# Revit family: Hager-Univers-IP30-D161-Cl.II-FWB-encl--CH-fr
name_source: partatom
category: Equipement électrique
units: mm (PartAtom-declared; Revit-internal decimal feet)

## family parameters
Configuration du panneau = Deux colonnes, circuits au sein
Cote de connecteur circulaire = Utiliser le diamètre
Couper avec des vides une fois chargée = Non
Hôte = Face
Partagée = Non
Point de calcul de pièce = Non
Type d'élément = Tableau de raccordement

## types (19) — shared parameters
Commentaires du type = Univers
EF000003 - mode de pose = EV000384 - saillie
EF000007 - couleur = EV000202 - blanc
EF000049 - profondeur = 161 mm  [stored 0.528215 ft]
EF000116 - numéro RAL = 9010
EF000118 - avec cadre/support de montage = Non
EF001088 - possibilité de montage en saillie = Oui
EF001596 - matériau du boîtier/corps = EV000179 - acier
EF001613 - maintien de fonction = EV000494 - sans
EF002950 - largeur en nombre de modules = 12
EF003532 - convient pour utilisation à l’extérieur = Non
EF004293 - indice de protection contre les chocs (IK) = EV006815 - IK09
EF004464 - type de porte = EV000494 - sans
EF005474 - indice de protection (IP) = EV006410 - IP30
EF006244 - couvercle/porte transparent(e) = Non
EF006306 - avec serrure = Non
EF007800 - adapté à un parafoudre = Non
EF008873 - courant nominal (In) = 125 A
EF015940 - couvercle avec décharge de pression = Non
Fabricant = Hager
HG000002 - avec porte = Non
HG000003 - Gamme = Univers
HG000006 - Encastré = Non
HG000009 - Porte à double battant = Non
HG000010 - Portes asymétriques = Non
HG000023 - Armoire double section = Non
HG000024 - Hauteur de la section basse = 800 mm  [stored 2.62467 ft]
HG000026 - Installation au sol = Non
zero-valued in all types: EF000218 - profondeur d'encastrement, EF000266 - nombre de rangées, Elévation par défaut, HG000027 - Hauteur du socle

## per-type parameters (varying)
| type | EF000008 - largeur | EF000040 - hauteur | EF000339 - type de capot | EF000437 - nombre d'entrées de conduit | EF001131 - profondeur intérieure | EF004427 - nombre de modules | EF009170 - épaisseur de matériau du boîtier | EF009171 - épaisseur de matériau de la porte/du couvercle | EF009212 - finition du couvercle | EF009554 - nombre d'ouvertures pour plaques à bride | HG000004 - Référence fabricant |
| saillie IP30 L1050 H1100 P161  - FWB74D1 | 1050 mm | 1100 mm | EV000494 - sans | 16 | 156 mm  [stored 0.511811 ft] | 336 | 1 mm  [stored 0.00328084 ft] | 1 mm  [stored 0.00328084 ft] | EV009916 - avec échancrure | 8 | FWB74D1 |
| saillie IP30 L1050 H500 P161  - FWB34D1 | 1050 mm | 500 mm  [stored 1.64042 ft] | EV000494 - sans | 16 | 156 mm  [stored 0.511811 ft] | 144 | 1 mm  [stored 0.00328084 ft] | 2 mm  [stored 0.00656168 ft] | EV009916 - avec échancrure | 8 | FWB34D1 |
| saillie IP30 L1050 H650 P161  - FWB44D1 | 1050 mm | 650 mm  [stored 2.13255 ft] | EV004216 - porte | 16 | 160 mm  [stored 0.524934 ft] | 192 | 1 mm  [stored 0.00328084 ft] | 1 mm  [stored 0.00328084 ft] | EV000116 - fermé | 8 | FWB44D1 |
| saillie IP30 L1050 H800 P161  - FWB54D1 | 1050 mm | 800 mm  [stored 2.62467 ft] | EV004216 - porte | 16 | 160 mm  [stored 0.524934 ft] | 240 | 2 mm  [stored 0.00656168 ft] | 1 mm  [stored 0.00328084 ft] | EV009916 - avec échancrure | 8 | FWB54D1 |
| saillie IP30 L1050 H950 P161  - FWB64D1 | 1050 mm | 950 mm  [stored 3.1168 ft] | EV004216 - porte | 16 | 160 mm  [stored 0.524934 ft] | 288 | 2 mm  [stored 0.00656168 ft] | 1 mm  [stored 0.00328084 ft] | EV009916 - avec échancrure | 8 | FWB64D1 |
| saillie IP30 L300 H1100 P161  - FWB71D1 | 300 mm | 1100 mm | EV000494 - sans | 4 | 156 mm  [stored 0.511811 ft] | 84 | 1 mm  [stored 0.00328084 ft] | 1 mm  [stored 0.00328084 ft] | EV009916 - avec échancrure | 2 | FWB71D1 |
| saillie IP30 L300 H1250 P161  - FWB81D1 | 300 mm | 1250 mm  [stored 4.10105 ft] | EV000494 - sans | 4 | 160 mm  [stored 0.524934 ft] | 96 | 1 mm  [stored 0.00328084 ft] | 1 mm  [stored 0.00328084 ft] | EV009916 - avec échancrure | 2 | FWB81D1 |
| saillie IP30 L300 H650 P161  - FWB41D1 | 300 mm | 650 mm  [stored 2.13255 ft] | EV004216 - porte | 4 | 160 mm  [stored 0.524934 ft] | 48 | 1 mm  [stored 0.00328084 ft] | 1 mm  [stored 0.00328084 ft] | EV000116 - fermé | 2 | FWB41D1 |
| saillie IP30 L300 H800 P161  - FWB51D1 | 300 mm | 800 mm  [stored 2.62467 ft] | EV000494 - sans | 4 | 156 mm  [stored 0.511811 ft] | 60 | 1 mm  [stored 0.00328084 ft] | 1 mm  [stored 0.00328084 ft] | EV009916 - avec échancrure | 2 | FWB51D1 |
| saillie IP30 L300 H950 P161  - FWB61D1 | 300 mm | 950 mm  [stored 3.1168 ft] | EV000494 - sans | 4 | 156 mm  [stored 0.511811 ft] | 72 | 1 mm  [stored 0.00328084 ft] | 1 mm  [stored 0.00328084 ft] | EV009916 - avec échancrure | 2 | FWB61D1 |
| saillie IP30 L550 H1100 P161  - FWB72D1 | 550 mm | 1100 mm | EV000494 - sans | 8 | 156 mm  [stored 0.511811 ft] | 168 | 1 mm  [stored 0.00328084 ft] | 1 mm  [stored 0.00328084 ft] | EV009916 - avec échancrure | 4 | FWB72D1 |
| saillie IP30 L550 H500 P161  - FWB32D1 | 550 mm | 500 mm  [stored 1.64042 ft] | EV000494 - sans | 8 | 156 mm  [stored 0.511811 ft] | 72 | 2 mm  [stored 0.00656168 ft] | 2 mm  [stored 0.00656168 ft] | EV009916 - avec échancrure | 4 | FWB32D1 |
| saillie IP30 L550 H650 P161  - FWB42D1 | 550 mm | 650 mm  [stored 2.13255 ft] | EV004216 - porte | 8 | 160 mm  [stored 0.524934 ft] | 96 | 1 mm  [stored 0.00328084 ft] | 1 mm  [stored 0.00328084 ft] | EV000116 - fermé | 4 | FWB42D1 |
| saillie IP30 L550 H800 P161  - FWB52D1 | 550 mm | 800 mm  [stored 2.62467 ft] | EV000494 - sans | 8 | 156 mm  [stored 0.511811 ft] | 120 | 1 mm  [stored 0.00328084 ft] | 1 mm  [stored 0.00328084 ft] | EV009916 - avec échancrure | 4 | FWB52D1 |
| saillie IP30 L550 H950 P161  - FWB62D1 | 550 mm | 950 mm  [stored 3.1168 ft] | EV000494 - sans | 8 | 156 mm  [stored 0.511811 ft] | 144 | 1 mm  [stored 0.00328084 ft] | 1 mm  [stored 0.00328084 ft] | EV009916 - avec échancrure | 4 | FWB62D1 |
| saillie IP30 L800 H500 P161  - FWB33D1 | 800 mm  [stored 2.62467 ft] | 500 mm  [stored 1.64042 ft] | EV004216 - porte | 12 | 160 mm  [stored 0.524934 ft] | 108 | 1 mm  [stored 0.00328084 ft] | 1 mm  [stored 0.00328084 ft] | EV000116 - fermé | 6 | FWB33D1 |
| saillie IP30 L800 H650 P161  - FWB43D1 | 800 mm  [stored 2.62467 ft] | 650 mm  [stored 2.13255 ft] | EV004216 - porte | 12 | 160 mm  [stored 0.524934 ft] | 144 | 2 mm  [stored 0.00656168 ft] | 1 mm  [stored 0.00328084 ft] | EV000116 - fermé | 6 | FWB43D1 |
| saillie IP30 L800 H800 P161  - FWB53D1 | 800 mm  [stored 2.62467 ft] | 800 mm  [stored 2.62467 ft] | EV004216 - porte | 12 | 160 mm  [stored 0.524934 ft] | 180 | 1 mm  [stored 0.00328084 ft] | 1 mm  [stored 0.00328084 ft] | EV000116 - fermé | 6 | FWB53D1 |
| saillie IP30 L800 H950 P161  - FWB63D1 | 800 mm  [stored 2.62467 ft] | 950 mm  [stored 3.1168 ft] | EV004216 - porte | 12 | 160 mm  [stored 0.524934 ft] | 216 | 2 mm  [stored 0.00656168 ft] | 1 mm  [stored 0.00328084 ft] | EV009916 - avec échancrure | 6 | FWB63D1 |

note: [stored X ft] marks values corroborated as IEEE doubles in the binary element streams (Revit-internal decimal feet)

## geometry (parser evidence)
native form markers: Sweep x10
no freeform markers — native parametric forms only
